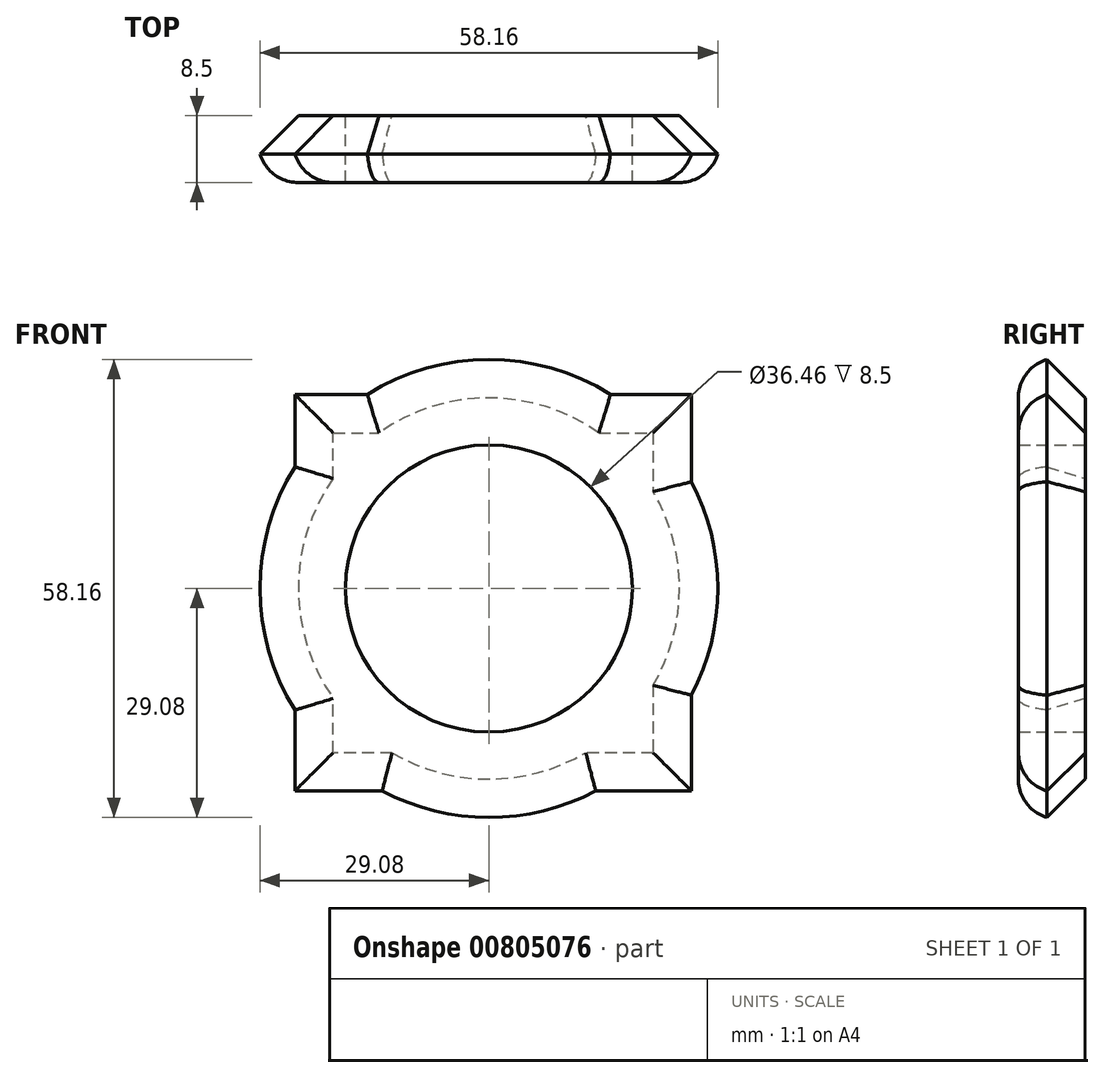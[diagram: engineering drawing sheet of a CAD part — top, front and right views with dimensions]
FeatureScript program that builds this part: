
annotation { "Feature Type Name" : "Feature", "Feature Type Description" : "" }
export const myFeature = defineFeature(function(context is Context, id is Id, definition is map)
    precondition{}
    {
        {
            var Q0;
            Q0=qCreatedBy(makeId("Front.planeOp"),FACE);
            var sketch = newSketch(context, id + "F0", { "sketchPlane" : qUnion([Q0])});
            skLineSegment(sketch, "E0.bottom", {"start": v(0, 0) * mm, "end": v(50.8, 0) * mm});
            skLineSegment(sketch, "E0.top", {"start": v(0, 50.8) * mm, "end": v(50.8, 50.8) * mm});
            skLineSegment(sketch, "E0.left", {"start": v(0, 0) * mm, "end": v(0, 50.8) * mm});
            skLineSegment(sketch, "E0.right", {"start": v(50.8, 0) * mm, "end": v(50.8, 50.8) * mm});
            skCircle(sketch, "E1", {"center": v(24.86, 25.94) * mm, "radius": 29.3 * mm});
            skCircle(sketch, "E2", {"center": v(24.86, 25.94) * mm, "radius": 18.23 * mm});
            skSolve(sketch);
        }
        {
            var Q0;
            Q0 = qSketchRegion(id + "F0", true);
            extrude(context, id + "F1", {"entities" : qUnion([Q0]), "depth" : 8.5 * mm, "offsetDistance" : 25.4 * mm});
        }
        {
            var Q0;
            {var subQ0=sQuery(id+"F0.wireOp",EDGE,"E1");var subQ1=sQuery(id+"F0.wireOp",EDGE,"E0.top");Q0=makeQuery(id+"F1.opExtrude","CAP_EDGE",EDGE,{"disambiguationData":[OSD([subQ0]),TDD([makeQuery(id+"F0.imprint","IMPRINT",EDGE,{"disambiguationData":[TD([[makeQuery(id+"F0.imprint","INTERSECT",VERTEX,{"disambiguationData":[OD(0.0)],"derivedFrom":[subQ1,subQ0]}),1.0]])],"derivedFrom":subQ0})])],"isStart":false});}
            var Q1;
            {var subQ0=sQuery(id+"F0.wireOp",EDGE,"E0.top");Q1=makeQuery(id+"F1.opExtrude","CAP_EDGE",EDGE,{"disambiguationData":[OSD([subQ0]),TDD([makeQuery(id+"F0.imprint","IMPRINT",EDGE,{"disambiguationData":[TD([[makeQuery(id+"F0.imprint","INTERSECT",VERTEX,{"derivedFrom":[subQ0,sQuery(id+"F0.wireOp",EDGE,"E0.left")]}),-1.0]])],"derivedFrom":subQ0})])],"isStart":false});}
            var Q2;
            {var subQ0=sQuery(id+"F0.wireOp",EDGE,"E0.top");Q2=makeQuery(id+"F1.opExtrude","CAP_EDGE",EDGE,{"disambiguationData":[OSD([subQ0]),TDD([makeQuery(id+"F0.imprint","IMPRINT",EDGE,{"disambiguationData":[TD([[makeQuery(id+"F0.imprint","INTERSECT",VERTEX,{"derivedFrom":[subQ0,sQuery(id+"F0.wireOp",EDGE,"E0.right")]}),1.0]])],"derivedFrom":subQ0})])],"isStart":false});}
            var Q3;
            {var subQ0=sQuery(id+"F0.wireOp",EDGE,"E0.right");Q3=makeQuery(id+"F1.opExtrude","CAP_EDGE",EDGE,{"disambiguationData":[OSD([subQ0]),TDD([makeQuery(id+"F0.imprint","IMPRINT",EDGE,{"disambiguationData":[TD([[makeQuery(id+"F0.imprint","INTERSECT",VERTEX,{"derivedFrom":[sQuery(id+"F0.wireOp",EDGE,"E0.top"),subQ0]}),1.0]])],"derivedFrom":subQ0})])],"isStart":false});}
            var Q4;
            {var subQ0=sQuery(id+"F0.wireOp",EDGE,"E1");var subQ1=sQuery(id+"F0.wireOp",EDGE,"E0.right");Q4=makeQuery(id+"F1.opExtrude","CAP_EDGE",EDGE,{"disambiguationData":[OSD([subQ0]),TDD([makeQuery(id+"F0.imprint","IMPRINT",EDGE,{"disambiguationData":[TD([[makeQuery(id+"F0.imprint","INTERSECT",VERTEX,{"disambiguationData":[OD(0.0)],"derivedFrom":[subQ1,subQ0]}),-1.0]])],"derivedFrom":subQ0})])],"isStart":false});}
            var Q5;
            {var subQ0=sQuery(id+"F0.wireOp",EDGE,"E0.right");Q5=makeQuery(id+"F1.opExtrude","CAP_EDGE",EDGE,{"disambiguationData":[OSD([subQ0]),TDD([makeQuery(id+"F0.imprint","IMPRINT",EDGE,{"disambiguationData":[TD([[makeQuery(id+"F0.imprint","INTERSECT",VERTEX,{"derivedFrom":[sQuery(id+"F0.wireOp",EDGE,"E0.bottom"),subQ0]}),-1.0]])],"derivedFrom":subQ0})])],"isStart":false});}
            var Q6;
            {var subQ0=sQuery(id+"F0.wireOp",EDGE,"E1");var subQ1=sQuery(id+"F0.wireOp",EDGE,"E0.bottom");Q6=makeQuery(id+"F1.opExtrude","CAP_EDGE",EDGE,{"disambiguationData":[OSD([subQ0]),TDD([makeQuery(id+"F0.imprint","IMPRINT",EDGE,{"disambiguationData":[TD([[makeQuery(id+"F0.imprint","INTERSECT",VERTEX,{"disambiguationData":[OD(0.0)],"derivedFrom":[subQ1,subQ0]}),-1.0]])],"derivedFrom":subQ0})])],"isStart":false});}
            var Q7;
            {var subQ0=sQuery(id+"F0.wireOp",EDGE,"E0.bottom");Q7=makeQuery(id+"F1.opExtrude","CAP_EDGE",EDGE,{"disambiguationData":[OSD([subQ0]),TDD([makeQuery(id+"F0.imprint","IMPRINT",EDGE,{"disambiguationData":[TD([[makeQuery(id+"F0.imprint","INTERSECT",VERTEX,{"derivedFrom":[subQ0,sQuery(id+"F0.wireOp",EDGE,"E0.right")]}),1.0]])],"derivedFrom":subQ0})])],"isStart":false});}
            var Q8;
            {var subQ0=sQuery(id+"F0.wireOp",EDGE,"E0.bottom");Q8=makeQuery(id+"F1.opExtrude","CAP_EDGE",EDGE,{"disambiguationData":[OSD([subQ0]),TDD([makeQuery(id+"F0.imprint","IMPRINT",EDGE,{"disambiguationData":[TD([[makeQuery(id+"F0.imprint","INTERSECT",VERTEX,{"derivedFrom":[subQ0,sQuery(id+"F0.wireOp",EDGE,"E0.left")]}),-1.0]])],"derivedFrom":subQ0})])],"isStart":false});}
            var Q9;
            {var subQ0=sQuery(id+"F0.wireOp",EDGE,"E0.left");Q9=makeQuery(id+"F1.opExtrude","CAP_EDGE",EDGE,{"disambiguationData":[OSD([subQ0]),TDD([makeQuery(id+"F0.imprint","IMPRINT",EDGE,{"disambiguationData":[TD([[makeQuery(id+"F0.imprint","INTERSECT",VERTEX,{"derivedFrom":[sQuery(id+"F0.wireOp",EDGE,"E0.bottom"),subQ0]}),-1.0]])],"derivedFrom":subQ0})])],"isStart":false});}
            var Q10;
            {var subQ0=sQuery(id+"F0.wireOp",EDGE,"E1");var subQ1=sQuery(id+"F0.wireOp",EDGE,"E0.left");Q10=makeQuery(id+"F1.opExtrude","CAP_EDGE",EDGE,{"disambiguationData":[OSD([subQ0]),TDD([makeQuery(id+"F0.imprint","IMPRINT",EDGE,{"disambiguationData":[TD([[makeQuery(id+"F0.imprint","INTERSECT",VERTEX,{"disambiguationData":[OD(0.0)],"derivedFrom":[subQ1,subQ0]}),1.0]])],"derivedFrom":subQ0})])],"isStart":false});}
            var Q11;
            {var subQ0=sQuery(id+"F0.wireOp",EDGE,"E0.left");Q11=makeQuery(id+"F1.opExtrude","CAP_EDGE",EDGE,{"disambiguationData":[OSD([subQ0]),TDD([makeQuery(id+"F0.imprint","IMPRINT",EDGE,{"disambiguationData":[TD([[makeQuery(id+"F0.imprint","INTERSECT",VERTEX,{"derivedFrom":[sQuery(id+"F0.wireOp",EDGE,"E0.top"),subQ0]}),1.0]])],"derivedFrom":subQ0})])],"isStart":false});}
            fillet(context, id + "F2", {"entities" : qUnion([Q0, Q1, Q2, Q3, Q4, Q5, Q6, Q7, Q8, Q9, Q10, Q11]), "radius" : 5.08 * mm, "tangentPropagation" : true, "allowEdgeOverflow" : false});
        }
        {
            var Q0;
            {var subQ0=sQuery(id+"F0.wireOp",EDGE,"E1");var subQ1=sQuery(id+"F0.wireOp",EDGE,"E0.left");Q0=makeQuery(id+"F1.opExtrude","CAP_EDGE",EDGE,{"disambiguationData":[OSD([subQ0]),TDD([makeQuery(id+"F0.imprint","IMPRINT",EDGE,{"disambiguationData":[TD([[makeQuery(id+"F0.imprint","INTERSECT",VERTEX,{"disambiguationData":[OD(0.0)],"derivedFrom":[subQ1,subQ0]}),1.0]])],"derivedFrom":subQ0})])],"isStart":true});}
            var Q1;
            {var subQ0=sQuery(id+"F0.wireOp",EDGE,"E0.left");Q1=makeQuery(id+"F1.opExtrude","CAP_EDGE",EDGE,{"disambiguationData":[OSD([subQ0]),TDD([makeQuery(id+"F0.imprint","IMPRINT",EDGE,{"disambiguationData":[TD([[makeQuery(id+"F0.imprint","INTERSECT",VERTEX,{"derivedFrom":[sQuery(id+"F0.wireOp",EDGE,"E0.bottom"),subQ0]}),-1.0]])],"derivedFrom":subQ0})])],"isStart":true});}
            var Q2;
            {var subQ0=sQuery(id+"F0.wireOp",EDGE,"E0.left");Q2=makeQuery(id+"F1.opExtrude","CAP_EDGE",EDGE,{"disambiguationData":[OSD([subQ0]),TDD([makeQuery(id+"F0.imprint","IMPRINT",EDGE,{"disambiguationData":[TD([[makeQuery(id+"F0.imprint","INTERSECT",VERTEX,{"derivedFrom":[sQuery(id+"F0.wireOp",EDGE,"E0.top"),subQ0]}),1.0]])],"derivedFrom":subQ0})])],"isStart":true});}
            var Q3;
            {var subQ0=sQuery(id+"F0.wireOp",EDGE,"E0.bottom");Q3=makeQuery(id+"F1.opExtrude","CAP_EDGE",EDGE,{"disambiguationData":[OSD([subQ0]),TDD([makeQuery(id+"F0.imprint","IMPRINT",EDGE,{"disambiguationData":[TD([[makeQuery(id+"F0.imprint","INTERSECT",VERTEX,{"derivedFrom":[subQ0,sQuery(id+"F0.wireOp",EDGE,"E0.left")]}),-1.0]])],"derivedFrom":subQ0})])],"isStart":true});}
            var Q4;
            {var subQ0=sQuery(id+"F0.wireOp",EDGE,"E1");var subQ1=sQuery(id+"F0.wireOp",EDGE,"E0.bottom");Q4=makeQuery(id+"F1.opExtrude","CAP_EDGE",EDGE,{"disambiguationData":[OSD([subQ0]),TDD([makeQuery(id+"F0.imprint","IMPRINT",EDGE,{"disambiguationData":[TD([[makeQuery(id+"F0.imprint","INTERSECT",VERTEX,{"disambiguationData":[OD(0.0)],"derivedFrom":[subQ1,subQ0]}),-1.0]])],"derivedFrom":subQ0})])],"isStart":true});}
            var Q5;
            {var subQ0=sQuery(id+"F0.wireOp",EDGE,"E0.bottom");Q5=makeQuery(id+"F1.opExtrude","CAP_EDGE",EDGE,{"disambiguationData":[OSD([subQ0]),TDD([makeQuery(id+"F0.imprint","IMPRINT",EDGE,{"disambiguationData":[TD([[makeQuery(id+"F0.imprint","INTERSECT",VERTEX,{"derivedFrom":[subQ0,sQuery(id+"F0.wireOp",EDGE,"E0.right")]}),1.0]])],"derivedFrom":subQ0})])],"isStart":true});}
            var Q6;
            {var subQ0=sQuery(id+"F0.wireOp",EDGE,"E0.right");Q6=makeQuery(id+"F1.opExtrude","CAP_EDGE",EDGE,{"disambiguationData":[OSD([subQ0]),TDD([makeQuery(id+"F0.imprint","IMPRINT",EDGE,{"disambiguationData":[TD([[makeQuery(id+"F0.imprint","INTERSECT",VERTEX,{"derivedFrom":[sQuery(id+"F0.wireOp",EDGE,"E0.bottom"),subQ0]}),-1.0]])],"derivedFrom":subQ0})])],"isStart":true});}
            var Q7;
            {var subQ0=sQuery(id+"F0.wireOp",EDGE,"E1");var subQ1=sQuery(id+"F0.wireOp",EDGE,"E0.right");Q7=makeQuery(id+"F1.opExtrude","CAP_EDGE",EDGE,{"disambiguationData":[OSD([subQ0]),TDD([makeQuery(id+"F0.imprint","IMPRINT",EDGE,{"disambiguationData":[TD([[makeQuery(id+"F0.imprint","INTERSECT",VERTEX,{"disambiguationData":[OD(0.0)],"derivedFrom":[subQ1,subQ0]}),-1.0]])],"derivedFrom":subQ0})])],"isStart":true});}
            var Q8;
            {var subQ0=sQuery(id+"F0.wireOp",EDGE,"E0.right");Q8=makeQuery(id+"F1.opExtrude","CAP_EDGE",EDGE,{"disambiguationData":[OSD([subQ0]),TDD([makeQuery(id+"F0.imprint","IMPRINT",EDGE,{"disambiguationData":[TD([[makeQuery(id+"F0.imprint","INTERSECT",VERTEX,{"derivedFrom":[sQuery(id+"F0.wireOp",EDGE,"E0.top"),subQ0]}),1.0]])],"derivedFrom":subQ0})])],"isStart":true});}
            var Q9;
            {var subQ0=sQuery(id+"F0.wireOp",EDGE,"E0.top");Q9=makeQuery(id+"F1.opExtrude","CAP_EDGE",EDGE,{"disambiguationData":[OSD([subQ0]),TDD([makeQuery(id+"F0.imprint","IMPRINT",EDGE,{"disambiguationData":[TD([[makeQuery(id+"F0.imprint","INTERSECT",VERTEX,{"derivedFrom":[subQ0,sQuery(id+"F0.wireOp",EDGE,"E0.right")]}),1.0]])],"derivedFrom":subQ0})])],"isStart":true});}
            var Q10;
            {var subQ0=sQuery(id+"F0.wireOp",EDGE,"E1");var subQ1=sQuery(id+"F0.wireOp",EDGE,"E0.top");Q10=makeQuery(id+"F1.opExtrude","CAP_EDGE",EDGE,{"disambiguationData":[OSD([subQ0]),TDD([makeQuery(id+"F0.imprint","IMPRINT",EDGE,{"disambiguationData":[TD([[makeQuery(id+"F0.imprint","INTERSECT",VERTEX,{"disambiguationData":[OD(0.0)],"derivedFrom":[subQ1,subQ0]}),1.0]])],"derivedFrom":subQ0})])],"isStart":true});}
            var Q11;
            {var subQ0=sQuery(id+"F0.wireOp",EDGE,"E0.top");Q11=makeQuery(id+"F1.opExtrude","CAP_EDGE",EDGE,{"disambiguationData":[OSD([subQ0]),TDD([makeQuery(id+"F0.imprint","IMPRINT",EDGE,{"disambiguationData":[TD([[makeQuery(id+"F0.imprint","INTERSECT",VERTEX,{"derivedFrom":[subQ0,sQuery(id+"F0.wireOp",EDGE,"E0.left")]}),-1.0]])],"derivedFrom":subQ0})])],"isStart":true});}
            chamfer(context, id + "F3", {"entities" : qUnion([Q0, Q1, Q2, Q3, Q4, Q5, Q6, Q7, Q8, Q9, Q10, Q11]), "width" : 5.08 * mm, "tangentPropagation" : true});
        }
    });
